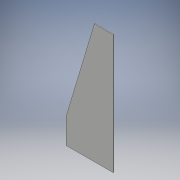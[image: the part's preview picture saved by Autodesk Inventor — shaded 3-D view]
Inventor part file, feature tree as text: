
AUTODESK INVENTOR PART (.ipt)
format: ipt  version: 2018 (Build 220112000, 112)  size: 95,232 bytes
history: native  units: mm
features: other x1, extrude x1, sketch x1
ambient origin geometry x8: Origin, YZ Plane, XZ Plane, XY Plane, X Axis, Y Axis, Z Axis, Center Point
bodies: Body1 (feature_tree)
feature tree (3):
  other  "ソリッド1"
  extrude  "押し出し1"  Depth=509.0mm
  sketch  "スケッチ1"
